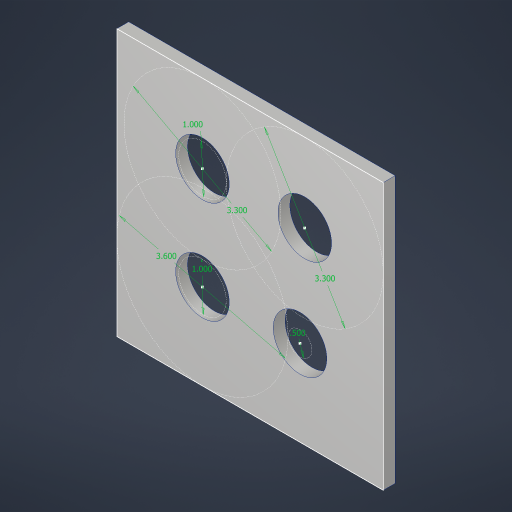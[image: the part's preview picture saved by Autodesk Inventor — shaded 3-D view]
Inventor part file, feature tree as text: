
AUTODESK INVENTOR PART (.ipt)
format: ipt  version: 2023.4 (Build 274418000, 418)  size: 188,928 bytes
history: native  units: in
note: dims shown in document units (in); Inventor stores cm internally (conversion verified against a paired STEP export)
features: sketch x1, extrude x1, hole x1
ambient origin geometry x8: Origin, YZ Plane, XZ Plane, XY Plane, X Axis, Y Axis, Z Axis, Center Point
bodies: Solid1 (feature_tree)
feature tree (3):
  sketch  "Sketch1"  dims[d0=0.5in d1=3.6in d2=1.0in d3=3.3in d4=1.0in d5=3.3in d6=0.25in d7=0.0in d8=1.125in d9=0.38in d10=0.375in d11=0.25in d12=0.5635in d13=1.0in d14=0.8108in]
  extrude  "Extrusion1"  Depth=0.25in
  hole  "Hole1"  [1 undecoded]
note: 1 required parameter value undecoded (feature->parameter linkage not recoverable at this tier; creation-order binding heuristic only, values carry confidence <= 0.55)
